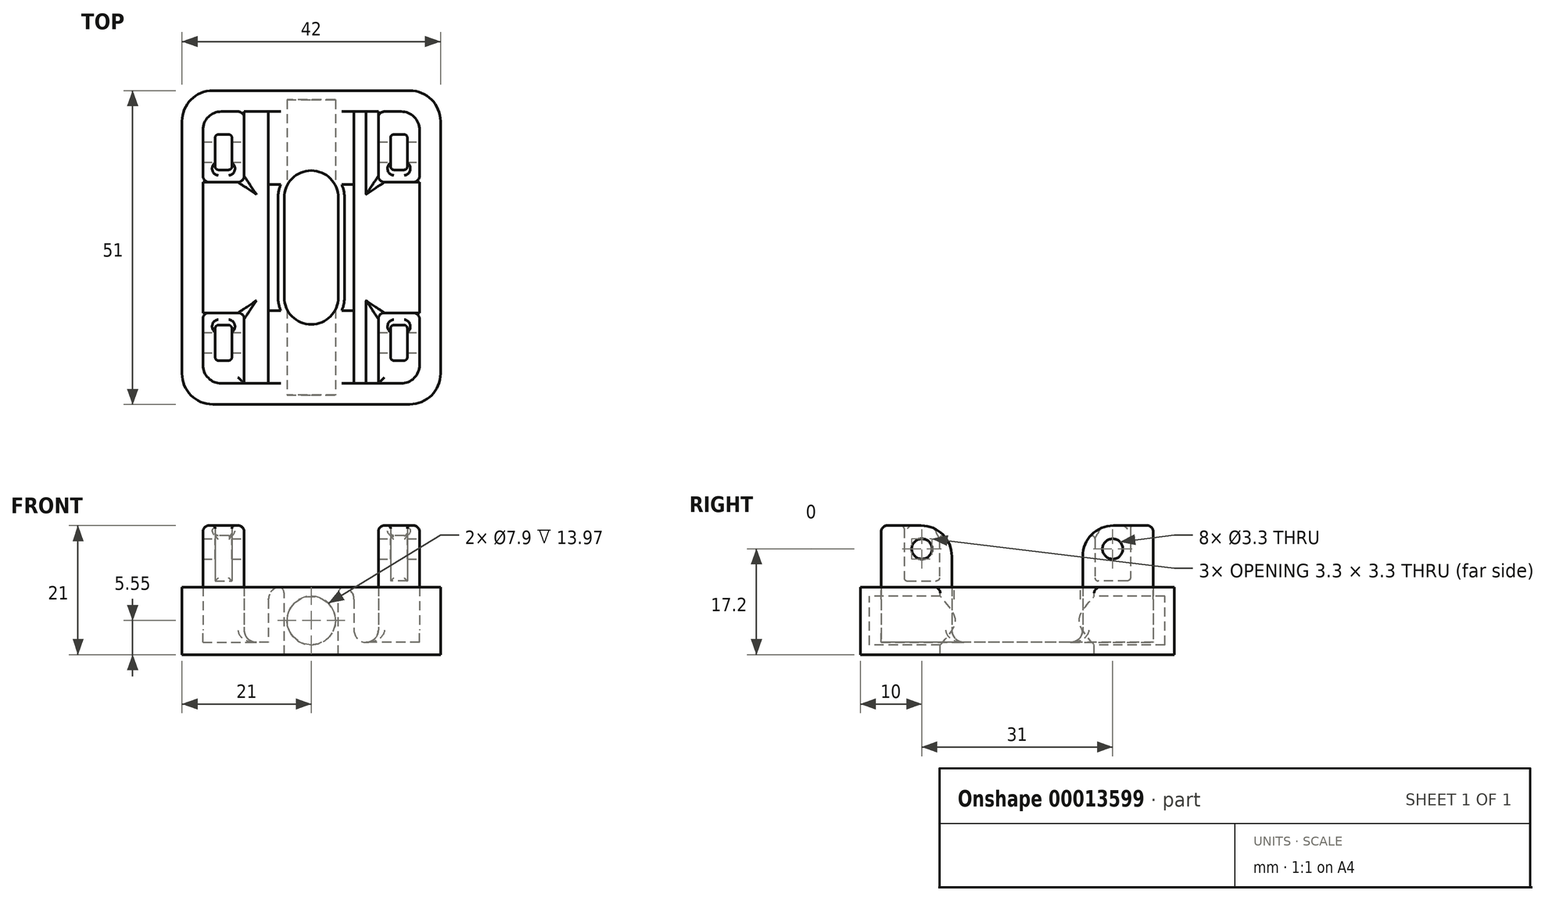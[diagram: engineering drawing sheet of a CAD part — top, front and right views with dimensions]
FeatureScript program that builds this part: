
annotation { "Feature Type Name" : "Feature", "Feature Type Description" : "" }
export const myFeature = defineFeature(function(context is Context, id is Id, definition is map)
    precondition{}
    {
        {
            var Q0;
            Q0=qCreatedBy(makeId("Top.planeOp"),FACE);
            var sketch = newSketch(context, id + "F0", { "sketchPlane" : qUnion([Q0])});
            skLineSegment(sketch, "E0.rect.bottom", {"start": v(18, 22.5) * mm, "end": v(-18, 22.5) * mm});
            skLineSegment(sketch, "E0.rect.top", {"start": v(18, -22.5) * mm, "end": v(-18, -22.5) * mm});
            skLineSegment(sketch, "E0.rect.left", {"start": v(18, 22.5) * mm, "end": v(18, -22.5) * mm});
            skLineSegment(sketch, "E0.rect.right", {"start": v(-18, 22.5) * mm, "end": v(-18, -22.5) * mm});
            skPoint(sketch, "E0.rect.middle", {"position": v(0, 0) * mm});
            skLineSegment(sketch, "E1.rect.bottom", {"start": v(21, 25.5) * mm, "end": v(-21, 25.5) * mm});
            skLineSegment(sketch, "E1.rect.top", {"start": v(21, -25.5) * mm, "end": v(-21, -25.5) * mm});
            skLineSegment(sketch, "E1.rect.left", {"start": v(21, 25.5) * mm, "end": v(21, -25.5) * mm});
            skLineSegment(sketch, "E1.rect.right", {"start": v(-21, 25.5) * mm, "end": v(-21, -25.5) * mm});
            skLineSegment(sketch, "E2.rect.bottom", {"start": v(17.6, 22.1) * mm, "end": v(-17.6, 22.1) * mm});
            skLineSegment(sketch, "E2.rect.top", {"start": v(17.6, -22.1) * mm, "end": v(-17.6, -22.1) * mm});
            skLineSegment(sketch, "E2.rect.left", {"start": v(17.6, 22.1) * mm, "end": v(17.6, -22.1) * mm});
            skLineSegment(sketch, "E2.rect.right", {"start": v(-17.6, 22.1) * mm, "end": v(-17.6, -22.1) * mm});
            skLineSegment(sketch, "E3", {"start": v(21, 15.5) * mm, "end": v(-21, 15.5) * mm, "construction": true});
            skLineSegment(sketch, "E4.rect.bottom", {"start": v(15.6, 18.37) * mm, "end": v(12.9, 18.37) * mm});
            skLineSegment(sketch, "E4.rect.top", {"start": v(15.6, 12.62) * mm, "end": v(12.9, 12.62) * mm});
            skLineSegment(sketch, "E4.rect.left", {"start": v(15.6, 18.37) * mm, "end": v(15.6, 12.63) * mm});
            skLineSegment(sketch, "E4.rect.right", {"start": v(12.9, 18.37) * mm, "end": v(12.9, 12.63) * mm});
            skPoint(sketch, "E4.rect.middle", {"position": v(14.25, 15.5) * mm});
            skLineSegment(sketch, "E5", {"start": v(17.6, 10.62) * mm, "end": v(10.9, 10.62) * mm});
            skLineSegment(sketch, "E6", {"start": v(10.9, 10.62) * mm, "end": v(10.9, 22.1) * mm});
            skLineSegment(sketch, "E7", {"start": v(0, 0) * mm, "end": v(0, 25.5) * mm, "construction": true});
            skLineSegment(sketch, "E8", {"start": v(0, 0) * mm, "end": v(21, 0) * mm, "construction": true});
            skLineSegment(sketch, "E9.0.MirrorCS", {"start": v(-12.9, 18.37) * mm, "end": v(-12.9, 12.63) * mm});
            skLineSegment(sketch, "E10.0.MirrorCS", {"start": v(-15.6, 18.38) * mm, "end": v(-12.9, 18.38) * mm});
            skLineSegment(sketch, "E11.0.MirrorCS", {"start": v(-15.6, 18.37) * mm, "end": v(-15.6, 12.63) * mm});
            skLineSegment(sketch, "E12.0.MirrorCS", {"start": v(-15.6, 12.62) * mm, "end": v(-12.9, 12.62) * mm});
            skLineSegment(sketch, "E13.0.MirrorCS", {"start": v(-17.6, 10.62) * mm, "end": v(-10.9, 10.62) * mm});
            skLineSegment(sketch, "E14.0.MirrorCS", {"start": v(-10.9, 10.62) * mm, "end": v(-10.9, 22.1) * mm});
            skLineSegment(sketch, "E15.0.MirrorCS", {"start": v(17.6, -10.62) * mm, "end": v(10.9, -10.62) * mm});
            skLineSegment(sketch, "E16.0.MirrorCS", {"start": v(10.9, -10.62) * mm, "end": v(10.9, -22.1) * mm});
            skLineSegment(sketch, "E17.0.MirrorCS", {"start": v(15.6, -12.62) * mm, "end": v(12.9, -12.62) * mm});
            skLineSegment(sketch, "E18.0.MirrorCS", {"start": v(15.6, -18.37) * mm, "end": v(15.6, -12.63) * mm});
            skLineSegment(sketch, "E19.0.MirrorCS", {"start": v(15.6, -18.38) * mm, "end": v(12.9, -18.38) * mm});
            skLineSegment(sketch, "E20.0.MirrorCS", {"start": v(12.9, -18.37) * mm, "end": v(12.9, -12.63) * mm});
            skLineSegment(sketch, "E21.0.MirrorCS", {"start": v(-10.9, -10.62) * mm, "end": v(-10.9, -22.1) * mm});
            skLineSegment(sketch, "E22.0.MirrorCS", {"start": v(-17.6, -10.62) * mm, "end": v(-10.9, -10.62) * mm});
            skLineSegment(sketch, "E23.0.MirrorCS", {"start": v(-15.6, -12.62) * mm, "end": v(-12.9, -12.62) * mm});
            skLineSegment(sketch, "E24.0.MirrorCS", {"start": v(-12.9, -18.37) * mm, "end": v(-12.9, -12.63) * mm});
            skLineSegment(sketch, "E25.0.MirrorCS", {"start": v(-15.6, -18.38) * mm, "end": v(-12.9, -18.38) * mm});
            skLineSegment(sketch, "E26.0.MirrorCS", {"start": v(-15.6, -18.37) * mm, "end": v(-15.6, -12.63) * mm});
            skLineSegment(sketch, "E27", {"start": v(3.95, 22.1) * mm, "end": v(3.95, -22.1) * mm, "construction": true});
            skLineSegment(sketch, "E28", {"start": v(-3.95, -22.1) * mm, "end": v(-3.95, 22.1) * mm, "construction": true});
            skLineSegment(sketch, "E29", {"start": v(-3.95, 17.1) * mm, "end": v(3.95, 17.1) * mm, "construction": true});
            skPoint(sketch, "E30", {"position": v(0, 17.1) * mm});
            skLineSegment(sketch, "E31", {"start": v(-6.95, 22.1) * mm, "end": v(-6.95, -22.1) * mm});
            skLineSegment(sketch, "E32", {"start": v(6.95, -22.1) * mm, "end": v(6.95, 22.1) * mm});
            skLineSegment(sketch, "E33.rect.bottom", {"start": v(4.4, 12.5) * mm, "end": v(-4.4, 12.5) * mm, "construction": true});
            skLineSegment(sketch, "E33.rect.top", {"start": v(4.4, -12.5) * mm, "end": v(-4.4, -12.5) * mm, "construction": true});
            skLineSegment(sketch, "E33.rect.left", {"start": v(4.4, 12.5) * mm, "end": v(4.4, -12.5) * mm});
            skLineSegment(sketch, "E33.rect.right", {"start": v(-4.4, 12.5) * mm, "end": v(-4.4, -12.5) * mm});
            skArc(sketch, "E34", {"start": v(4.4, 8.1) * mm, "mid": v(0, 12.5) * mm, "end": v(-4.4, 8.1) * mm});
            skArc(sketch, "E35", {"start": v(-4.4, -8.1) * mm, "mid": v(0, -12.5) * mm, "end": v(4.4, -8.1) * mm});
            skSolve(sketch);
        }
        {
            var Q0;
            Q0=makeQuery(id+"F0.imprint","IMPRINT",FACE,{"disambiguationData":[TD([[makeQuery(id+"F0.imprint","IMPRINT",EDGE,{"derivedFrom":sQuery(id+"F0.wireOp",EDGE,"E0.rect.bottom")}),-1.0]])]});
            var Q1;
            Q1=makeQuery(id+"F0.imprint","IMPRINT",FACE,{"disambiguationData":[TD([[makeQuery(id+"F0.imprint","IMPRINT",EDGE,{"derivedFrom":sQuery(id+"F0.wireOp",EDGE,"E0.rect.bottom")}),1.0]])]});
            var Q2;
            {var subQ5=sQuery(id+"F0.wireOp",EDGE,"E13.0.MirrorCS");Q2=makeQuery(id+"F0.imprint","IMPRINT",FACE,{"disambiguationData":[TD([[makeQuery(id+"F0.imprint","IMPRINT",EDGE,{"derivedFrom":subQ5}),-1.0]])]});}
            var Q3;
            Q3=makeQuery(id+"F0.imprint","IMPRINT",FACE,{"disambiguationData":[TD([[makeQuery(id+"F0.imprint","IMPRINT",EDGE,{"derivedFrom":sQuery(id+"F0.wireOp",EDGE,"E9.0.MirrorCS")}),1.0]])]});
            var Q4;
            Q4=makeQuery(id+"F0.imprint","IMPRINT",FACE,{"disambiguationData":[TD([[makeQuery(id+"F0.imprint","IMPRINT",EDGE,{"derivedFrom":sQuery(id+"F0.wireOp",EDGE,"E9.0.MirrorCS")}),-1.0]])]});
            var Q5;
            Q5=makeQuery(id+"F0.imprint","IMPRINT",FACE,{"disambiguationData":[TD([[makeQuery(id+"F0.imprint","IMPRINT",EDGE,{"derivedFrom":sQuery(id+"F0.wireOp",EDGE,"E23.0.MirrorCS")}),-1.0]])]});
            var Q6;
            {var subQ1=sQuery(id+"F0.wireOp",EDGE,"E21.0.MirrorCS");Q6=makeQuery(id+"F0.imprint","IMPRINT",FACE,{"disambiguationData":[TD([[makeQuery(id+"F0.imprint","IMPRINT",EDGE,{"derivedFrom":subQ1}),-1.0]])]});}
            var Q7;
            {var subQ5=sQuery(id+"F0.wireOp",EDGE,"E31");Q7=makeQuery(id+"F0.imprint","IMPRINT",FACE,{"disambiguationData":[TD([[makeQuery(id+"F0.imprint","IMPRINT",EDGE,{"derivedFrom":subQ5}),1.0]])]});}
            var Q8;
            {var subQ4=sQuery(id+"F0.wireOp",EDGE,"E5");Q8=makeQuery(id+"F0.imprint","IMPRINT",FACE,{"disambiguationData":[TD([[makeQuery(id+"F0.imprint","IMPRINT",EDGE,{"derivedFrom":subQ4}),1.0]])]});}
            var Q9;
            Q9=makeQuery(id+"F0.imprint","IMPRINT",FACE,{"disambiguationData":[TD([[makeQuery(id+"F0.imprint","IMPRINT",EDGE,{"derivedFrom":sQuery(id+"F0.wireOp",EDGE,"E4.rect.bottom")}),-1.0]])]});
            var Q10;
            Q10=makeQuery(id+"F0.imprint","IMPRINT",FACE,{"disambiguationData":[TD([[makeQuery(id+"F0.imprint","IMPRINT",EDGE,{"derivedFrom":sQuery(id+"F0.wireOp",EDGE,"E4.rect.bottom")}),1.0]])]});
            var Q11;
            Q11=makeQuery(id+"F0.imprint","IMPRINT",FACE,{"disambiguationData":[TD([[makeQuery(id+"F0.imprint","IMPRINT",EDGE,{"derivedFrom":sQuery(id+"F0.wireOp",EDGE,"E17.0.MirrorCS")}),1.0]])]});
            var Q12;
            {var subQ1=sQuery(id+"F0.wireOp",EDGE,"E15.0.MirrorCS");Q12=makeQuery(id+"F0.imprint","IMPRINT",FACE,{"disambiguationData":[TD([[makeQuery(id+"F0.imprint","IMPRINT",EDGE,{"derivedFrom":subQ1}),1.0]])]});}
            extrude(context, id + "F1", {"entities" : qUnion([Q0, Q1, Q2, Q3, Q4, Q5, Q6, Q7, Q8, Q9, Q10, Q11, Q12]), "oppositeDirection" : true, "depth" : 2 * mm});
        }
        {
            var Q0;
            Q0=makeQuery(id+"F0.imprint","IMPRINT",FACE,{"disambiguationData":[TD([[makeQuery(id+"F0.imprint","IMPRINT",EDGE,{"derivedFrom":sQuery(id+"F0.wireOp",EDGE,"E0.rect.bottom")}),1.0]])]});
            var Q1;
            Q1=makeQuery(id+"F0.imprint","IMPRINT",FACE,{"disambiguationData":[TD([[makeQuery(id+"F0.imprint","IMPRINT",EDGE,{"derivedFrom":sQuery(id+"F0.wireOp",EDGE,"E0.rect.bottom")}),-1.0]])]});
            extrude(context, id + "F2", {"entities" : qUnion([Q0, Q1]), "operationType" : NewBodyOperationType.ADD, "depth" : 9 * mm});
        }
        {
            var Q0;
            {var subQ1=sQuery(id+"F0.wireOp",EDGE,"E21.0.MirrorCS");Q0=makeQuery(id+"F0.imprint","IMPRINT",FACE,{"disambiguationData":[TD([[makeQuery(id+"F0.imprint","IMPRINT",EDGE,{"derivedFrom":subQ1}),-1.0]])]});}
            var Q1;
            Q1=makeQuery(id+"F0.imprint","IMPRINT",FACE,{"disambiguationData":[TD([[makeQuery(id+"F0.imprint","IMPRINT",EDGE,{"derivedFrom":sQuery(id+"F0.wireOp",EDGE,"E9.0.MirrorCS")}),1.0]])]});
            var Q2;
            Q2=makeQuery(id+"F0.imprint","IMPRINT",FACE,{"disambiguationData":[TD([[makeQuery(id+"F0.imprint","IMPRINT",EDGE,{"derivedFrom":sQuery(id+"F0.wireOp",EDGE,"E4.rect.bottom")}),-1.0]])]});
            var Q3;
            {var subQ1=sQuery(id+"F0.wireOp",EDGE,"E15.0.MirrorCS");Q3=makeQuery(id+"F0.imprint","IMPRINT",FACE,{"disambiguationData":[TD([[makeQuery(id+"F0.imprint","IMPRINT",EDGE,{"derivedFrom":subQ1}),1.0]])]});}
            extrude(context, id + "F3", {"entities" : qUnion([Q0, Q1, Q2, Q3]), "operationType" : NewBodyOperationType.ADD, "depth" : (10 + 9) * mm});
        }
        {
            var Q0;
            Q0=makeQuery(id+"F0.imprint","IMPRINT",FACE,{"disambiguationData":[TD([[makeQuery(id+"F0.imprint","IMPRINT",EDGE,{"derivedFrom":sQuery(id+"F0.wireOp",EDGE,"E17.0.MirrorCS")}),1.0]])]});
            var Q1;
            Q1=makeQuery(id+"F0.imprint","IMPRINT",FACE,{"disambiguationData":[TD([[makeQuery(id+"F0.imprint","IMPRINT",EDGE,{"derivedFrom":sQuery(id+"F0.wireOp",EDGE,"E23.0.MirrorCS")}),-1.0]])]});
            var Q2;
            Q2=makeQuery(id+"F0.imprint","IMPRINT",FACE,{"disambiguationData":[TD([[makeQuery(id+"F0.imprint","IMPRINT",EDGE,{"derivedFrom":sQuery(id+"F0.wireOp",EDGE,"E9.0.MirrorCS")}),-1.0]])]});
            var Q3;
            Q3=makeQuery(id+"F0.imprint","IMPRINT",FACE,{"disambiguationData":[TD([[makeQuery(id+"F0.imprint","IMPRINT",EDGE,{"derivedFrom":sQuery(id+"F0.wireOp",EDGE,"E4.rect.bottom")}),1.0]])]});
            extrude(context, id + "F4", {"entities" : qUnion([Q0, Q1, Q2, Q3]), "operationType" : NewBodyOperationType.ADD, "depth" : 10 * mm});
        }
        {
            var Q0;
            {var subQ0=sQuery(id+"F0.wireOp",EDGE,"E2.rect.left");Q0=makeQuery(id+"F3.opExtrude","SWEPT_FACE",FACE,{"disambiguationData":[OSD([subQ0]),TDD([makeQuery(id+"F0.imprint","IMPRINT",EDGE,{"disambiguationData":[TD([[makeQuery(id+"F0.imprint","INTERSECT",VERTEX,{"derivedFrom":[sQuery(id+"F0.wireOp",EDGE,"E2.rect.top"),subQ0]}),1.0]])],"derivedFrom":subQ0})])]});}
            var sketch = newSketch(context, id + "F5", { "sketchPlane" : qUnion([Q0])});
            skLineSegment(sketch, "E36.0", {"start": v(-18.38, 19) * mm, "end": v(-12.63, 19) * mm});
            skLineSegment(sketch, "E37.0", {"start": v(18.37, 19) * mm, "end": v(12.63, 19) * mm});
            skLineSegment(sketch, "E38", {"start": v(-15.5, 19) * mm, "end": v(-15.5, 15.2) * mm, "construction": true});
            skCircle(sketch, "E39", {"center": v(-15.5, 15.2) * mm, "radius": 1.65 * mm});
            skLineSegment(sketch, "E40", {"start": v(15.5, 19) * mm, "end": v(15.5, 15.2) * mm, "construction": true});
            skCircle(sketch, "E41", {"center": v(15.5, 15.2) * mm, "radius": 1.65 * mm});
            skSolve(sketch);
        }
        {
            var Q0;
            Q0=makeQuery(id+"F5.imprint","IMPRINT",FACE,{"disambiguationData":[TD([[makeQuery(id+"F5.imprint","IMPRINT",EDGE,{"derivedFrom":sQuery(id+"F5.wireOp",EDGE,"E39")}),1.0]])]});
            var Q1;
            Q1=makeQuery(id+"F5.imprint","IMPRINT",FACE,{"disambiguationData":[TD([[makeQuery(id+"F5.imprint","IMPRINT",EDGE,{"derivedFrom":sQuery(id+"F5.wireOp",EDGE,"E41")}),1.0]])]});
            extrude(context, id + "F6", {"entities" : qUnion([Q0, Q1]), "operationType" : NewBodyOperationType.REMOVE, "endBound" : BoundingType.THROUGH_ALL, "oppositeDirection" : true, "depth" : 25 * mm});
        }
        {
            var Q0;
            {var subQ5=sQuery(id+"F0.wireOp",EDGE,"E31");Q0=makeQuery(id+"F0.imprint","IMPRINT",FACE,{"disambiguationData":[TD([[makeQuery(id+"F0.imprint","IMPRINT",EDGE,{"derivedFrom":subQ5}),1.0]])]});}
            extrude(context, id + "F7", {"entities" : qUnion([Q0]), "operationType" : NewBodyOperationType.ADD, "depth" : 9 * mm});
        }
        {
            var Q0;
            Q0=qCreatedBy(makeId("Front.planeOp"),FACE);
            var sketch = newSketch(context, id + "F8", { "sketchPlane" : qUnion([Q0])});
            skLineSegment(sketch, "E42", {"start": v(0, 0) * mm, "end": v(0, 3.55) * mm, "construction": true});
            skCircle(sketch, "E43", {"center": v(0, 3.55) * mm, "radius": 3.95 * mm});
            skLineSegment(sketch, "E44.0", {"start": v(21, 9) * mm, "end": v(-21, 9) * mm});
            skSolve(sketch);
        }
        {
            var Q0;
            Q0=makeQuery(id+"F8.imprint","IMPRINT",FACE,{"disambiguationData":[TD([[makeQuery(id+"F8.imprint","IMPRINT",EDGE,{"derivedFrom":sQuery(id+"F8.wireOp",EDGE,"E43")}),1.0]])]});
            extrude(context, id + "F9", {"entities" : qUnion([Q0]), "operationType" : NewBodyOperationType.REMOVE, "endBound" : BoundingType.SYMMETRIC, "oppositeDirection" : true, "depth" : 48 * mm});
        }
        {
            var Q0;
            Q0=makeQuery(id+"F3.opExtrude","SWEPT_EDGE",EDGE,{"disambiguationData":[OSD([sQuery(id+"F0.wireOp",EDGE,"E2.rect.top"),sQuery(id+"F0.wireOp",EDGE,"E2.rect.left")])]});
            var Q1;
            Q1=makeQuery(id+"F3.opExtrude","SWEPT_EDGE",EDGE,{"disambiguationData":[OSD([sQuery(id+"F0.wireOp",EDGE,"E2.rect.top"),sQuery(id+"F0.wireOp",EDGE,"E2.rect.right")])]});
            var Q2;
            Q2=makeQuery(id+"F3.opExtrude","SWEPT_EDGE",EDGE,{"disambiguationData":[OSD([sQuery(id+"F0.wireOp",EDGE,"E2.rect.bottom"),sQuery(id+"F0.wireOp",EDGE,"E2.rect.right")])]});
            var Q3;
            Q3=makeQuery(id+"F3.opExtrude","SWEPT_EDGE",EDGE,{"disambiguationData":[OSD([sQuery(id+"F0.wireOp",EDGE,"E2.rect.bottom"),sQuery(id+"F0.wireOp",EDGE,"E2.rect.left")])]});
            fillet(context, id + "F10", {"entities" : qUnion([Q0, Q1, Q2, Q3]), "radius" : 3 * mm, "tangentPropagation" : true, "allowEdgeOverflow" : false});
        }
        {
            var Q0;
            {var subQ0=sQuery(id+"F0.wireOp",EDGE,"E1.rect.bottom");var subQ1=sQuery(id+"F0.wireOp",EDGE,"E1.rect.left");Q0=makeQuery(id+"F2.boolean.opBoolean","MERGE",EDGE,{"derivedFrom":[makeQuery(id+"F1.opExtrude","SWEPT_EDGE",EDGE,{"disambiguationData":[OSD([subQ0,subQ1])]}),makeQuery(id+"F2.opExtrude","SWEPT_EDGE",EDGE,{"disambiguationData":[OSD([subQ0,subQ1])]})]});}
            var Q1;
            {var subQ0=sQuery(id+"F0.wireOp",EDGE,"E1.rect.bottom");var subQ1=sQuery(id+"F0.wireOp",EDGE,"E1.rect.right");Q1=makeQuery(id+"F2.boolean.opBoolean","MERGE",EDGE,{"derivedFrom":[makeQuery(id+"F1.opExtrude","SWEPT_EDGE",EDGE,{"disambiguationData":[OSD([subQ0,subQ1])]}),makeQuery(id+"F2.opExtrude","SWEPT_EDGE",EDGE,{"disambiguationData":[OSD([subQ0,subQ1])]})]});}
            var Q2;
            {var subQ0=sQuery(id+"F0.wireOp",EDGE,"E1.rect.top");var subQ1=sQuery(id+"F0.wireOp",EDGE,"E1.rect.left");Q2=makeQuery(id+"F2.boolean.opBoolean","MERGE",EDGE,{"derivedFrom":[makeQuery(id+"F1.opExtrude","SWEPT_EDGE",EDGE,{"disambiguationData":[OSD([subQ0,subQ1])]}),makeQuery(id+"F2.opExtrude","SWEPT_EDGE",EDGE,{"disambiguationData":[OSD([subQ0,subQ1])]})]});}
            var Q3;
            {var subQ0=sQuery(id+"F0.wireOp",EDGE,"E1.rect.top");var subQ1=sQuery(id+"F0.wireOp",EDGE,"E1.rect.right");Q3=makeQuery(id+"F2.boolean.opBoolean","MERGE",EDGE,{"derivedFrom":[makeQuery(id+"F1.opExtrude","SWEPT_EDGE",EDGE,{"disambiguationData":[OSD([subQ0,subQ1])]}),makeQuery(id+"F2.opExtrude","SWEPT_EDGE",EDGE,{"disambiguationData":[OSD([subQ0,subQ1])]})]});}
            fillet(context, id + "F11", {"entities" : qUnion([Q0, Q1, Q2, Q3]), "radius" : 5 * mm, "tangentPropagation" : true, "allowEdgeOverflow" : false});
        }
        {
            var Q0;
            Q0=makeQuery(id+"F7.opExtrude","CAP_EDGE",EDGE,{"disambiguationData":[OSD([sQuery(id+"F0.wireOp",EDGE,"E35")])],"isStart":false});
            fillet(context, id + "F12", {"entities" : qUnion([Q0]), "radius" : 1 * mm, "tangentPropagation" : true, "allowEdgeOverflow" : false});
        }
        {
            var Q0;
            Q0=makeQuery(id+"F7.opExtrude","CAP_EDGE",EDGE,{"disambiguationData":[OSD([sQuery(id+"F0.wireOp",EDGE,"E32")])],"isStart":false});
            var Q1;
            Q1=makeQuery(id+"F7.opExtrude","CAP_EDGE",EDGE,{"disambiguationData":[OSD([sQuery(id+"F0.wireOp",EDGE,"E31")])],"isStart":false});
            var Q2;
            Q2=makeQuery(id+"F7.opExtrude","CAP_EDGE",EDGE,{"disambiguationData":[OSD([sQuery(id+"F0.wireOp",EDGE,"E32")])],"isStart":true});
            var Q3;
            Q3=makeQuery(id+"F7.opExtrude","CAP_EDGE",EDGE,{"disambiguationData":[OSD([sQuery(id+"F0.wireOp",EDGE,"E31")])],"isStart":true});
            var Q4;
            Q4=makeQuery(id+"F3.opExtrude","CAP_EDGE",EDGE,{"disambiguationData":[OSD([sQuery(id+"F0.wireOp",EDGE,"E21.0.MirrorCS")])],"isStart":true});
            var Q5;
            Q5=makeQuery(id+"F3.opExtrude","CAP_EDGE",EDGE,{"disambiguationData":[OSD([sQuery(id+"F0.wireOp",EDGE,"E22.0.MirrorCS")])],"isStart":true});
            var Q6;
            Q6=makeQuery(id+"F3.opExtrude","CAP_EDGE",EDGE,{"disambiguationData":[OSD([sQuery(id+"F0.wireOp",EDGE,"E14.0.MirrorCS")])],"isStart":true});
            var Q7;
            Q7=makeQuery(id+"F3.opExtrude","CAP_EDGE",EDGE,{"disambiguationData":[OSD([sQuery(id+"F0.wireOp",EDGE,"E13.0.MirrorCS")])],"isStart":true});
            var Q8;
            Q8=makeQuery(id+"F3.opExtrude","CAP_EDGE",EDGE,{"disambiguationData":[OSD([sQuery(id+"F0.wireOp",EDGE,"E16.0.MirrorCS")])],"isStart":true});
            var Q9;
            Q9=makeQuery(id+"F3.opExtrude","CAP_EDGE",EDGE,{"disambiguationData":[OSD([sQuery(id+"F0.wireOp",EDGE,"E15.0.MirrorCS")])],"isStart":true});
            var Q10;
            Q10=makeQuery(id+"F3.opExtrude","CAP_EDGE",EDGE,{"disambiguationData":[OSD([sQuery(id+"F0.wireOp",EDGE,"E5")])],"isStart":true});
            var Q11;
            Q11=makeQuery(id+"F3.opExtrude","CAP_EDGE",EDGE,{"disambiguationData":[OSD([sQuery(id+"F0.wireOp",EDGE,"E6")])],"isStart":true});
            fillet(context, id + "F13", {"entities" : qUnion([Q0, Q1, Q2, Q3, Q4, Q5, Q6, Q7, Q8, Q9, Q10, Q11]), "radius" : 2 * mm, "tangentPropagation" : true, "allowEdgeOverflow" : false});
        }
        {
            var Q0;
            Q0=makeQuery(id+"F3.opExtrude","CAP_EDGE",EDGE,{"disambiguationData":[OSD([sQuery(id+"F0.wireOp",EDGE,"E15.0.MirrorCS")])],"isStart":false});
            var Q1;
            Q1=makeQuery(id+"F3.opExtrude","CAP_EDGE",EDGE,{"disambiguationData":[OSD([sQuery(id+"F0.wireOp",EDGE,"E5")])],"isStart":false});
            var Q2;
            Q2=makeQuery(id+"F3.opExtrude","CAP_EDGE",EDGE,{"disambiguationData":[OSD([sQuery(id+"F0.wireOp",EDGE,"E13.0.MirrorCS")])],"isStart":false});
            var Q3;
            Q3=makeQuery(id+"F3.opExtrude","CAP_EDGE",EDGE,{"disambiguationData":[OSD([sQuery(id+"F0.wireOp",EDGE,"E22.0.MirrorCS")])],"isStart":false});
            fillet(context, id + "F14", {"entities" : qUnion([Q0, Q1, Q2, Q3]), "radius" : 5 * mm, "tangentPropagation" : true, "allowEdgeOverflow" : false});
        }
        {
            var Q0;
            {var subQ0=sQuery(id+"F0.wireOp",EDGE,"E2.rect.left");var subQ1=sQuery(id+"F0.wireOp",EDGE,"E15.0.MirrorCS");var subQ3=sQuery(id+"F0.wireOp",EDGE,"E1.rect.bottom");var subQ4=sQuery(id+"F0.wireOp",EDGE,"E1.rect.top");var subQ5=sQuery(id+"F0.wireOp",EDGE,"E1.rect.left");var subQ6=sQuery(id+"F0.wireOp",EDGE,"E1.rect.right");Q0=makeQuery(id+"F3.boolean.opBoolean","SPLIT",EDGE,{"disambiguationData":[TD([makeQuery(id+"F1.opExtrude","CAP_FACE",FACE,{"disambiguationData":[OSD([subQ3,subQ4,subQ5,subQ6,sQuery(id+"F0.wireOp",EDGE,"E33.rect.left"),sQuery(id+"F0.wireOp",EDGE,"E33.rect.right"),sQuery(id+"F0.wireOp",EDGE,"E34"),sQuery(id+"F0.wireOp",EDGE,"E35")])],"isStart":true})])],"derivedFrom":makeQuery(id+"F3.opExtrude","SWEPT_EDGE",EDGE,{"disambiguationData":[OSD([subQ0,subQ1])]})});}
            var Q1;
            {var subQ0=sQuery(id+"F0.wireOp",EDGE,"E2.rect.right");var subQ1=sQuery(id+"F0.wireOp",EDGE,"E22.0.MirrorCS");var subQ3=sQuery(id+"F0.wireOp",EDGE,"E1.rect.bottom");var subQ4=sQuery(id+"F0.wireOp",EDGE,"E1.rect.top");var subQ5=sQuery(id+"F0.wireOp",EDGE,"E1.rect.left");var subQ6=sQuery(id+"F0.wireOp",EDGE,"E1.rect.right");Q1=makeQuery(id+"F3.boolean.opBoolean","SPLIT",EDGE,{"disambiguationData":[TD([makeQuery(id+"F1.opExtrude","CAP_FACE",FACE,{"disambiguationData":[OSD([subQ3,subQ4,subQ5,subQ6,sQuery(id+"F0.wireOp",EDGE,"E33.rect.left"),sQuery(id+"F0.wireOp",EDGE,"E33.rect.right"),sQuery(id+"F0.wireOp",EDGE,"E34"),sQuery(id+"F0.wireOp",EDGE,"E35")])],"isStart":true})])],"derivedFrom":makeQuery(id+"F3.opExtrude","SWEPT_EDGE",EDGE,{"disambiguationData":[OSD([subQ0,subQ1])]})});}
            var Q2;
            Q2=makeQuery(id+"F3.opExtrude","SWEPT_EDGE",EDGE,{"disambiguationData":[OSD([sQuery(id+"F0.wireOp",EDGE,"E15.0.MirrorCS"),sQuery(id+"F0.wireOp",EDGE,"E16.0.MirrorCS")])]});
            var Q3;
            Q3=makeQuery(id+"F3.opExtrude","SWEPT_EDGE",EDGE,{"disambiguationData":[OSD([sQuery(id+"F0.wireOp",EDGE,"E5"),sQuery(id+"F0.wireOp",EDGE,"E6")])]});
            var Q4;
            Q4=makeQuery(id+"F3.opExtrude","SWEPT_EDGE",EDGE,{"disambiguationData":[OSD([sQuery(id+"F0.wireOp",EDGE,"E13.0.MirrorCS"),sQuery(id+"F0.wireOp",EDGE,"E14.0.MirrorCS")])]});
            var Q5;
            Q5=makeQuery(id+"F3.opExtrude","SWEPT_EDGE",EDGE,{"disambiguationData":[OSD([sQuery(id+"F0.wireOp",EDGE,"E21.0.MirrorCS"),sQuery(id+"F0.wireOp",EDGE,"E22.0.MirrorCS")])]});
            fillet(context, id + "F15", {"entities" : qUnion([Q0, Q1, Q2, Q3, Q4, Q5]), "radius" : 1 * mm, "tangentPropagation" : true, "allowEdgeOverflow" : false});
        }
        {
            var Q0;
            {var subQ0=sQuery(id+"F0.wireOp",EDGE,"E2.rect.left");Q0=makeQuery(id+"F3.opExtrude","CAP_EDGE",EDGE,{"disambiguationData":[OSD([subQ0]),TDD([makeQuery(id+"F0.imprint","IMPRINT",EDGE,{"disambiguationData":[TD([[makeQuery(id+"F0.imprint","INTERSECT",VERTEX,{"derivedFrom":[sQuery(id+"F0.wireOp",EDGE,"E2.rect.top"),subQ0]}),1.0]])],"derivedFrom":subQ0})])],"isStart":false});}
            var Q1;
            {var subQ0=sQuery(id+"F0.wireOp",EDGE,"E2.rect.right");Q1=makeQuery(id+"F3.opExtrude","CAP_EDGE",EDGE,{"disambiguationData":[OSD([subQ0]),TDD([makeQuery(id+"F0.imprint","IMPRINT",EDGE,{"disambiguationData":[TD([[makeQuery(id+"F0.imprint","INTERSECT",VERTEX,{"derivedFrom":[sQuery(id+"F0.wireOp",EDGE,"E2.rect.top"),subQ0]}),1.0]])],"derivedFrom":subQ0})])],"isStart":false});}
            var Q2;
            {var subQ0=sQuery(id+"F0.wireOp",EDGE,"E2.rect.right");Q2=makeQuery(id+"F3.opExtrude","CAP_EDGE",EDGE,{"disambiguationData":[OSD([subQ0]),TDD([makeQuery(id+"F0.imprint","IMPRINT",EDGE,{"disambiguationData":[TD([[makeQuery(id+"F0.imprint","INTERSECT",VERTEX,{"derivedFrom":[sQuery(id+"F0.wireOp",EDGE,"E2.rect.bottom"),subQ0]}),-1.0]])],"derivedFrom":subQ0})])],"isStart":false});}
            var Q3;
            {var subQ0=sQuery(id+"F0.wireOp",EDGE,"E2.rect.left");Q3=makeQuery(id+"F3.opExtrude","CAP_EDGE",EDGE,{"disambiguationData":[OSD([subQ0]),TDD([makeQuery(id+"F0.imprint","IMPRINT",EDGE,{"disambiguationData":[TD([[makeQuery(id+"F0.imprint","INTERSECT",VERTEX,{"derivedFrom":[sQuery(id+"F0.wireOp",EDGE,"E2.rect.bottom"),subQ0]}),-1.0]])],"derivedFrom":subQ0})])],"isStart":false});}
            fillet(context, id + "F16", {"entities" : qUnion([Q0, Q1, Q2, Q3]), "radius" : 1 * mm, "tangentPropagation" : true, "allowEdgeOverflow" : false});
        }
        {
            var Q0;
            Q0=makeQuery(id+"F3.opExtrude","SWEPT_FACE",FACE,{"disambiguationData":[OSD([sQuery(id+"F0.wireOp",EDGE,"E17.0.MirrorCS")])]});
            var Q1;
            Q1=makeQuery(id+"F3.opExtrude","SWEPT_FACE",FACE,{"disambiguationData":[OSD([sQuery(id+"F0.wireOp",EDGE,"E19.0.MirrorCS")])]});
            var Q2;
            Q2=makeQuery(id+"F3.opExtrude","SWEPT_FACE",FACE,{"disambiguationData":[OSD([sQuery(id+"F0.wireOp",EDGE,"E25.0.MirrorCS")])]});
            var Q3;
            Q3=makeQuery(id+"F3.opExtrude","SWEPT_FACE",FACE,{"disambiguationData":[OSD([sQuery(id+"F0.wireOp",EDGE,"E23.0.MirrorCS")])]});
            var Q4;
            Q4=makeQuery(id+"F3.opExtrude","SWEPT_FACE",FACE,{"disambiguationData":[OSD([sQuery(id+"F0.wireOp",EDGE,"E12.0.MirrorCS")])]});
            var Q5;
            Q5=makeQuery(id+"F3.opExtrude","SWEPT_FACE",FACE,{"disambiguationData":[OSD([sQuery(id+"F0.wireOp",EDGE,"E10.0.MirrorCS")])]});
            var Q6;
            Q6=makeQuery(id+"F3.opExtrude","SWEPT_FACE",FACE,{"disambiguationData":[OSD([sQuery(id+"F0.wireOp",EDGE,"E4.rect.top")])]});
            var Q7;
            Q7=makeQuery(id+"F3.opExtrude","SWEPT_FACE",FACE,{"disambiguationData":[OSD([sQuery(id+"F0.wireOp",EDGE,"E4.rect.bottom")])]});
            fillet(context, id + "F17", {"entities" : qUnion([Q0, Q1, Q2, Q3, Q4, Q5, Q6, Q7]), "radius" : 0.5 * mm, "tangentPropagation" : true, "allowEdgeOverflow" : false});
        }
    });
